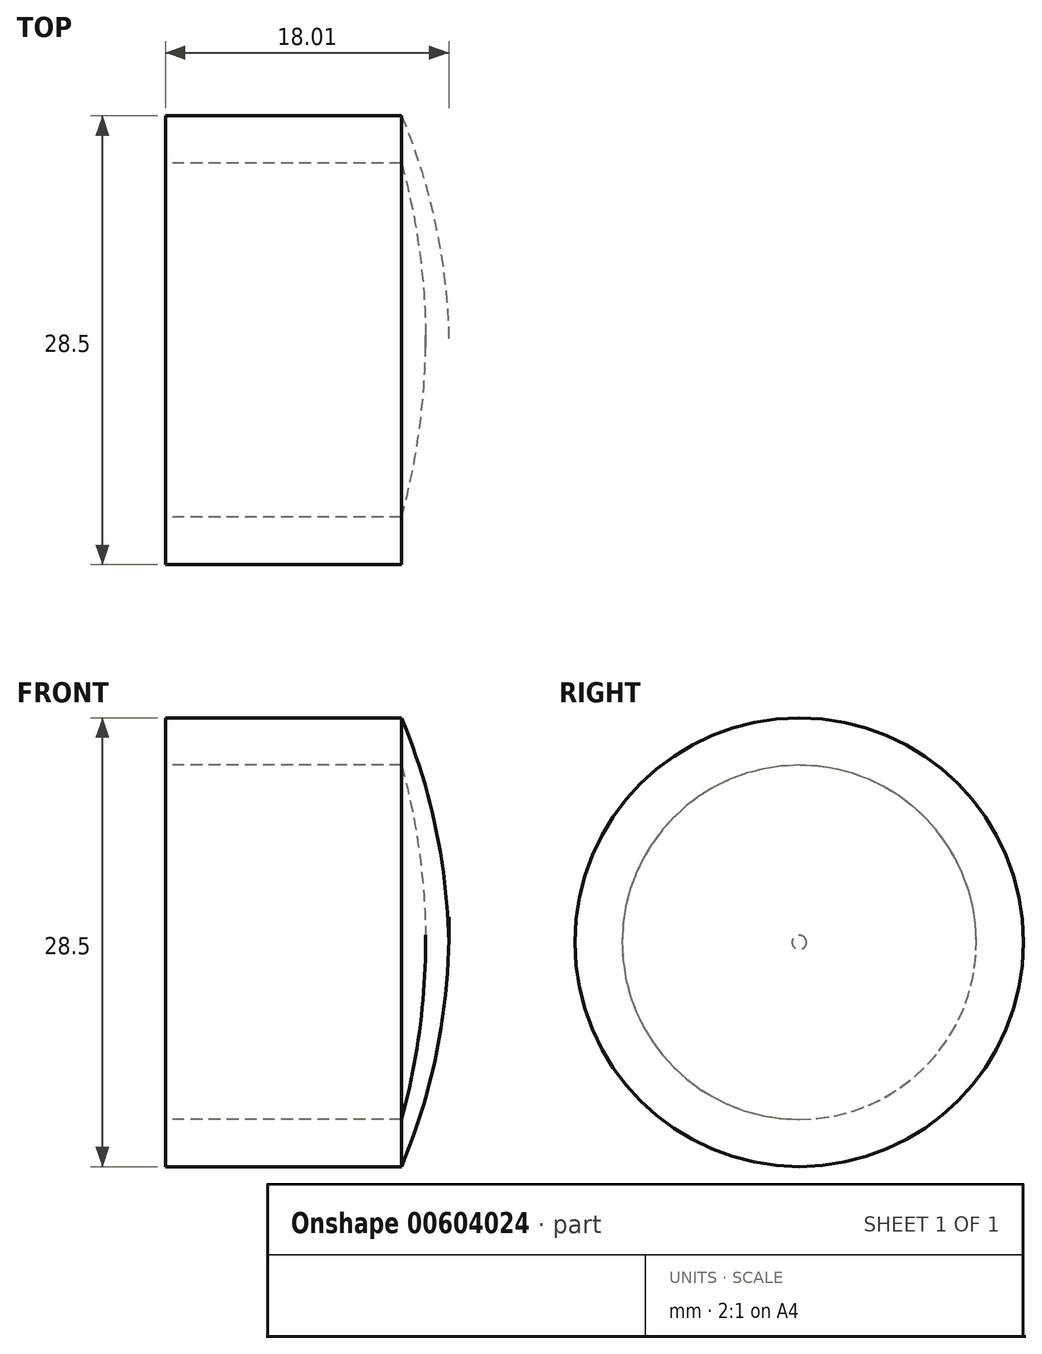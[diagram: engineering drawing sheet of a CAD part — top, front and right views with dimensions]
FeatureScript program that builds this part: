
annotation { "Feature Type Name" : "Feature", "Feature Type Description" : "" }
export const myFeature = defineFeature(function(context is Context, id is Id, definition is map)
    precondition{}
    {
        {
            var Q0;
            Q0=qCreatedBy(makeId("Top.planeOp"),FACE);
            var sketch = newSketch(context, id + "F0", { "sketchPlane" : qUnion([Q0])});
            skLineSegment(sketch, "E0.bottom", {"start": v(0, 11.25) * mm, "end": v(15, 11.25) * mm});
            skLineSegment(sketch, "E0.top", {"start": v(0, 14.25) * mm, "end": v(15, 14.25) * mm});
            skLineSegment(sketch, "E0.left", {"start": v(0, 11.25) * mm, "end": v(0, 14.25) * mm});
            skLineSegment(sketch, "E0.right", {"start": v(15, 11.25) * mm, "end": v(15, 14.25) * mm});
            skPoint(sketch, "E1.bottom.start.orphan", {"position": v(19.15, 0) * mm});
            skArc(sketch, "E2", {"start": v(18, 0) * mm, "mid": v(17.17, 7.27) * mm, "end": v(15, 14.25) * mm});
            skArc(sketch, "E3", {"start": v(16.53, 0) * mm, "mid": v(16.13, 5.68) * mm, "end": v(15, 11.25) * mm});
            skLineSegment(sketch, "E4", {"start": v(18, 0) * mm, "end": v(16.53, 0) * mm});
            skLineSegment(sketch, "E5", {"start": v(0, 0) * mm, "end": v(24.35, 0) * mm, "construction": true});
            skSolve(sketch);
        }
        {
            var Q0;
            Q0=makeQuery(id+"F0.imprint","IMPRINT",FACE,{"disambiguationData":[TD([[makeQuery(id+"F0.imprint","IMPRINT",EDGE,{"derivedFrom":sQuery(id+"F0.wireOp",EDGE,"E0.bottom")}),1.0]])]});
            var Q1;
            Q1=makeQuery(id+"F0.imprint","IMPRINT",FACE,{"disambiguationData":[TD([[makeQuery(id+"F0.imprint","IMPRINT",EDGE,{"derivedFrom":sQuery(id+"F0.wireOp",EDGE,"E0.right")}),-1.0]])]});
            var Q2;
            Q2=sQuery(id+"F0.wireOp",EDGE,"E5");
            revolve(context, id + "F1", {"entities" : qUnion([Q0, Q1]), "axis" : qUnion([Q2]), "revolveType" : RevolveType.FULL});
        }
    });
